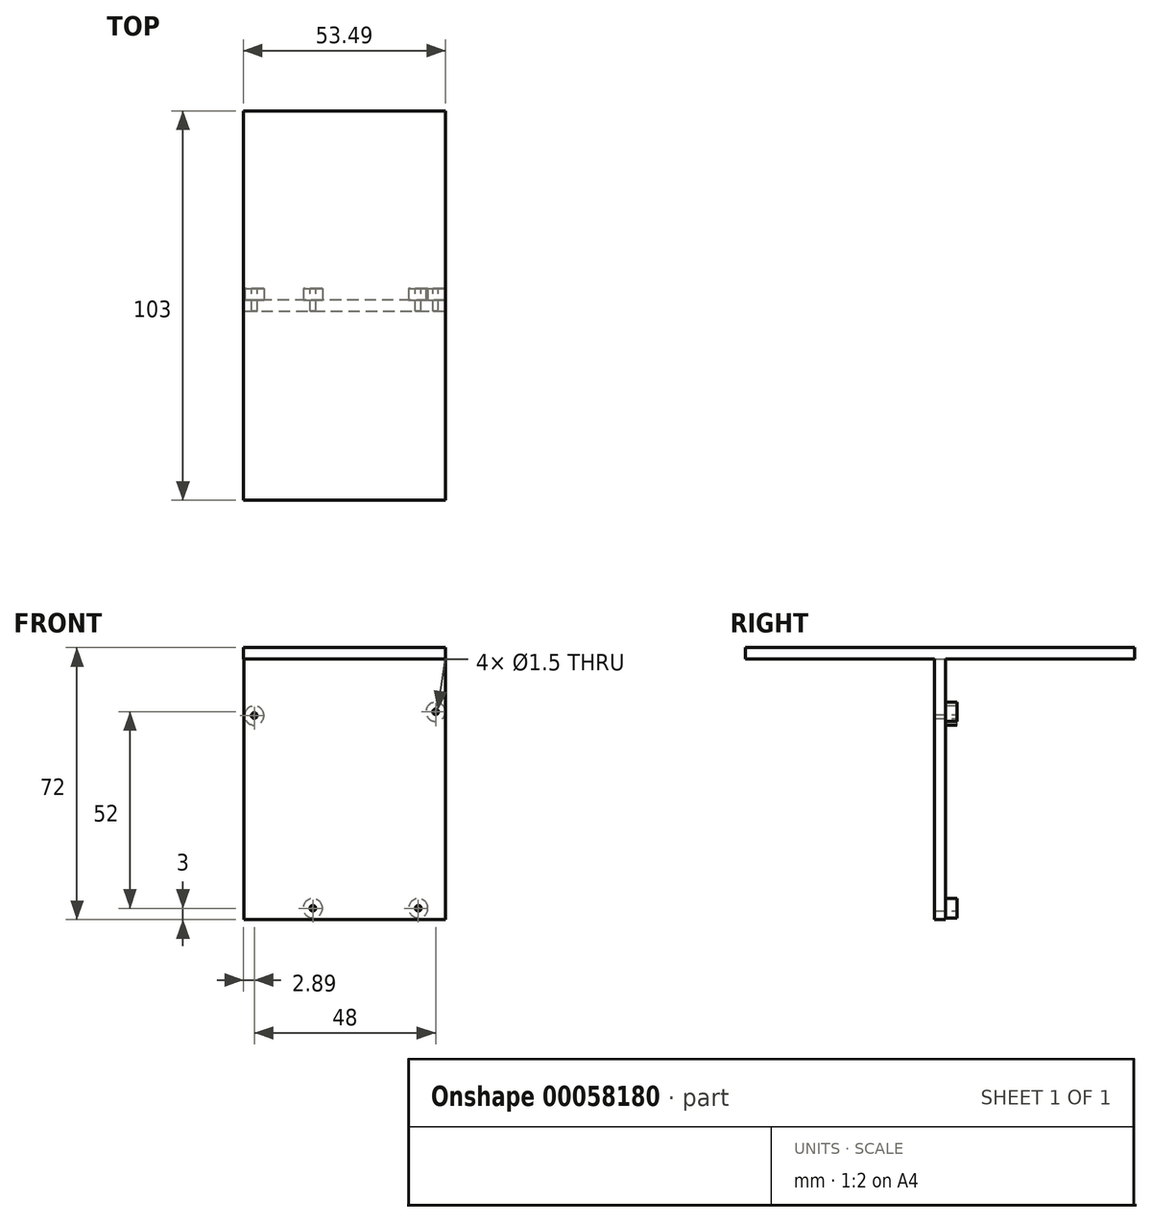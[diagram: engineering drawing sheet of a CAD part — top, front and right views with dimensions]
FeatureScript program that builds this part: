
annotation { "Feature Type Name" : "Feature", "Feature Type Description" : "" }
export const myFeature = defineFeature(function(context is Context, id is Id, definition is map)
    precondition{}
    {
        {
            var Q0;
            Q0=qCreatedBy(makeId("Front.planeOp"),FACE);
            var sketch = newSketch(context, id + "F0", { "sketchPlane" : qUnion([Q0])});
            skLineSegment(sketch, "E0.top", {"start": v(-53.3, -72) * mm, "end": v(0, -72) * mm});
            skLineSegment(sketch, "E0.left", {"start": v(-53.3, 0) * mm, "end": v(-53.3, -72) * mm});
            skLineSegment(sketch, "E0.right", {"start": v(0, 0) * mm, "end": v(0, -72) * mm});
            skCircle(sketch, "E1", {"center": v(-50.6, -18) * mm, "radius": 2.55 * mm});
            skCircle(sketch, "E2", {"center": v(-2.6, -17) * mm, "radius": 2.55 * mm});
            skCircle(sketch, "E3", {"center": v(-7.2, -69) * mm, "radius": 2.55 * mm});
            skCircle(sketch, "E4", {"center": v(-35.1, -69) * mm, "radius": 2.55 * mm});
            skLineSegment(sketch, "E5", {"start": v(-53.3, 0) * mm, "end": v(0, 0) * mm});
            skCircle(sketch, "E6", {"center": v(-2.6, -17) * mm, "radius": 0.75 * mm});
            skCircle(sketch, "E7", {"center": v(-50.6, -18) * mm, "radius": 0.75 * mm});
            skCircle(sketch, "E8", {"center": v(-7.2, -69) * mm, "radius": 0.75 * mm});
            skCircle(sketch, "E9", {"center": v(-35.1, -69) * mm, "radius": 0.75 * mm});
            skSolve(sketch);
        }
        {
            var Q0;
            {var subQ1=sQuery(id+"F0.wireOp",EDGE,"E0.top");Q0=makeQuery(id+"F0.imprint","IMPRINT",FACE,{"disambiguationData":[TD([[makeQuery(id+"F0.imprint","IMPRINT",EDGE,{"derivedFrom":subQ1}),1.0]])]});}
            var Q1;
            Q1=makeQuery(id+"F0.imprint","IMPRINT",FACE,{"disambiguationData":[TD([[makeQuery(id+"F0.imprint","IMPRINT",EDGE,{"derivedFrom":sQuery(id+"F0.wireOp",EDGE,"E1")}),1.0]])]});
            var Q2;
            Q2=makeQuery(id+"F0.imprint","IMPRINT",FACE,{"disambiguationData":[TD([[makeQuery(id+"F0.imprint","IMPRINT",EDGE,{"derivedFrom":sQuery(id+"F0.wireOp",EDGE,"E2")}),1.0]])]});
            var Q3;
            Q3=makeQuery(id+"F0.imprint","IMPRINT",FACE,{"disambiguationData":[TD([[makeQuery(id+"F0.imprint","IMPRINT",EDGE,{"derivedFrom":sQuery(id+"F0.wireOp",EDGE,"E3")}),1.0]])]});
            var Q4;
            Q4=makeQuery(id+"F0.imprint","IMPRINT",FACE,{"disambiguationData":[TD([[makeQuery(id+"F0.imprint","IMPRINT",EDGE,{"derivedFrom":sQuery(id+"F0.wireOp",EDGE,"E4")}),1.0]])]});
            extrude(context, id + "F1", {"entities" : qUnion([Q0, Q1, Q2, Q3, Q4]), "depth" : 3 * mm});
        }
        {
            var Q0;
            Q0=makeQuery(id+"F0.imprint","IMPRINT",FACE,{"disambiguationData":[TD([[makeQuery(id+"F0.imprint","IMPRINT",EDGE,{"derivedFrom":sQuery(id+"F0.wireOp",EDGE,"E1")}),1.0]])]});
            var Q1;
            Q1=makeQuery(id+"F0.imprint","IMPRINT",FACE,{"disambiguationData":[TD([[makeQuery(id+"F0.imprint","IMPRINT",EDGE,{"derivedFrom":sQuery(id+"F0.wireOp",EDGE,"E2")}),1.0]])]});
            var Q2;
            Q2=makeQuery(id+"F0.imprint","IMPRINT",FACE,{"disambiguationData":[TD([[makeQuery(id+"F0.imprint","IMPRINT",EDGE,{"derivedFrom":sQuery(id+"F0.wireOp",EDGE,"E3")}),1.0]])]});
            var Q3;
            Q3=makeQuery(id+"F0.imprint","IMPRINT",FACE,{"disambiguationData":[TD([[makeQuery(id+"F0.imprint","IMPRINT",EDGE,{"derivedFrom":sQuery(id+"F0.wireOp",EDGE,"E4")}),1.0]])]});
            extrude(context, id + "F2", {"entities" : qUnion([Q0, Q1, Q2, Q3]), "operationType" : NewBodyOperationType.ADD, "oppositeDirection" : true, "depth" : 3 * mm});
        }
        {
            var Q0;
            Q0=makeQuery(id+"F0.imprint","IMPRINT",FACE,{"disambiguationData":[TD([[makeQuery(id+"F0.imprint","IMPRINT",EDGE,{"derivedFrom":sQuery(id+"F0.wireOp",EDGE,"E6")}),1.0]])]});
            var Q1;
            Q1=makeQuery(id+"F0.imprint","IMPRINT",FACE,{"disambiguationData":[TD([[makeQuery(id+"F0.imprint","IMPRINT",EDGE,{"derivedFrom":sQuery(id+"F0.wireOp",EDGE,"E7")}),1.0]])]});
            var Q2;
            Q2=makeQuery(id+"F0.imprint","IMPRINT",FACE,{"disambiguationData":[TD([[makeQuery(id+"F0.imprint","IMPRINT",EDGE,{"derivedFrom":sQuery(id+"F0.wireOp",EDGE,"E9")}),1.0]])]});
            var Q3;
            Q3=makeQuery(id+"F0.imprint","IMPRINT",FACE,{"disambiguationData":[TD([[makeQuery(id+"F0.imprint","IMPRINT",EDGE,{"derivedFrom":sQuery(id+"F0.wireOp",EDGE,"E8")}),1.0]])]});
            extrude(context, id + "F3", {"entities" : qUnion([Q0, Q1, Q2, Q3]), "operationType" : NewBodyOperationType.REMOVE, "oppositeDirection" : true, "depth" : 3 * mm});
        }
        {
            var Q0;
            Q0=qCreatedBy(makeId("Front.planeOp"),FACE);
            var sketch = newSketch(context, id + "F4", { "sketchPlane" : qUnion([Q0])});
            skLineSegment(sketch, "E10.bottom", {"start": v(0, 0) * mm, "end": v(-53.5, 0) * mm});
            skLineSegment(sketch, "E10.top", {"start": v(0, -3) * mm, "end": v(-53.5, -3) * mm});
            skLineSegment(sketch, "E10.left", {"start": v(0, 0) * mm, "end": v(0, -3) * mm});
            skLineSegment(sketch, "E10.right", {"start": v(-53.5, 0) * mm, "end": v(-53.5, -3) * mm});
            skSolve(sketch);
        }
        {
            var Q0;
            Q0=makeQuery(id+"F4.imprint","IMPRINT",FACE,{"disambiguationData":[TD([[makeQuery(id+"F4.imprint","IMPRINT",EDGE,{"derivedFrom":sQuery(id+"F4.wireOp",EDGE,"E10.bottom")}),1.0]])]});
            extrude(context, id + "F5", {"entities" : qUnion([Q0]), "operationType" : NewBodyOperationType.ADD, "depth" : 53 * mm});
        }
        {
            var Q0;
            Q0=makeQuery(id+"F4.imprint","IMPRINT",FACE,{"disambiguationData":[TD([[makeQuery(id+"F4.imprint","IMPRINT",EDGE,{"derivedFrom":sQuery(id+"F4.wireOp",EDGE,"E10.bottom")}),1.0]])]});
            extrude(context, id + "F6", {"entities" : qUnion([Q0]), "operationType" : NewBodyOperationType.ADD, "oppositeDirection" : true, "depth" : 50 * mm});
        }
    });
